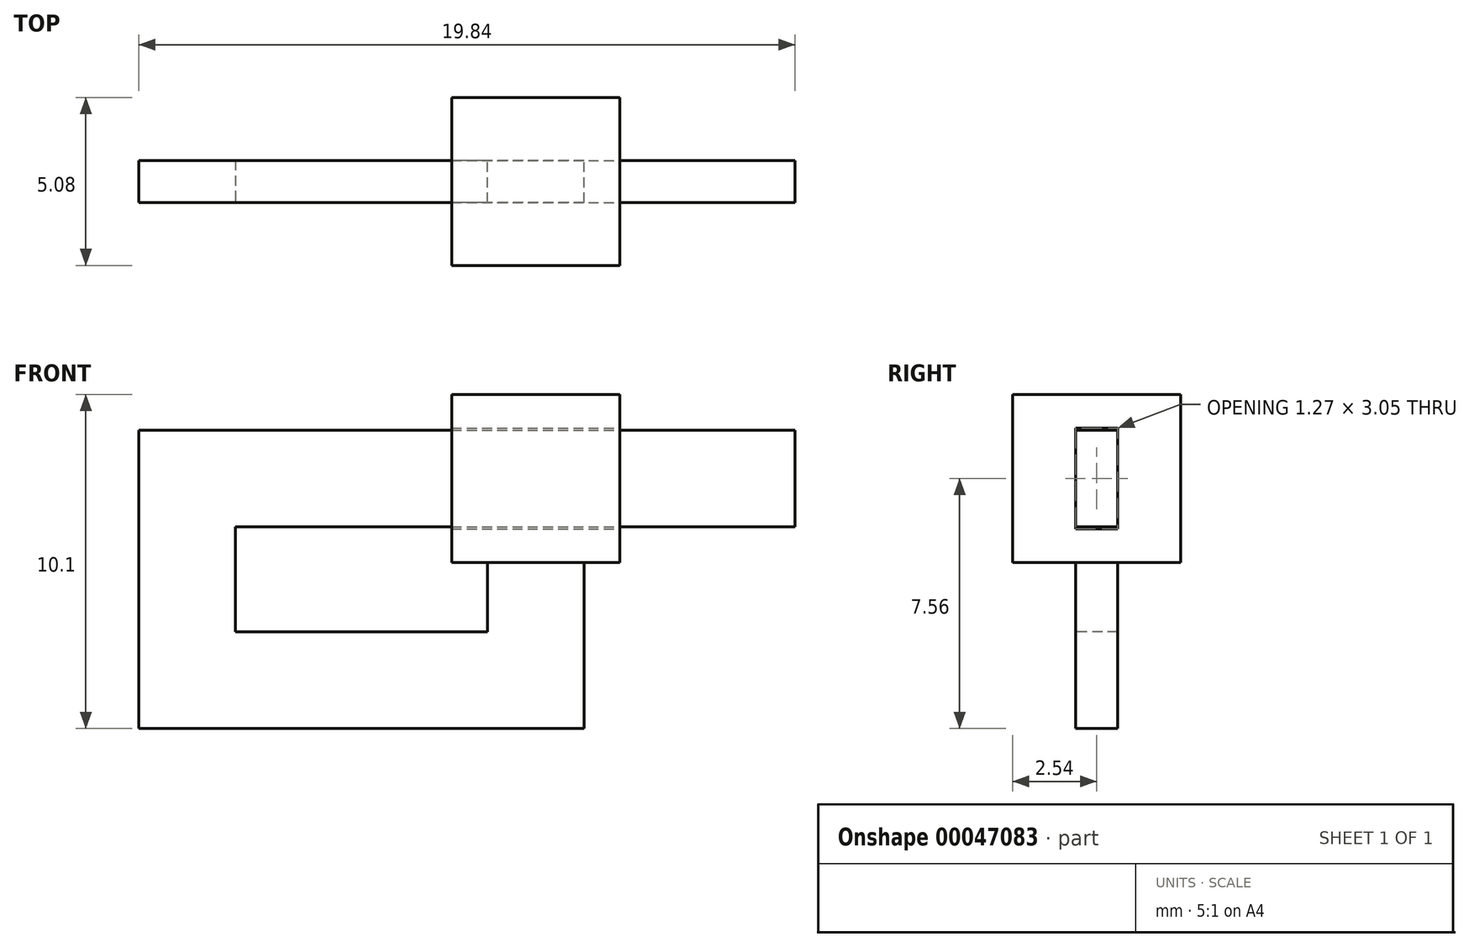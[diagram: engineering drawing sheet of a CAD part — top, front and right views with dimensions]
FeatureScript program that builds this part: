
annotation { "Feature Type Name" : "Feature", "Feature Type Description" : "" }
export const myFeature = defineFeature(function(context is Context, id is Id, definition is map)
    precondition{}
    {
        {
            var Q0;
            Q0=qCreatedBy(makeId("Right.planeOp"),FACE);
            var sketch = newSketch(context, id + "F0", { "sketchPlane" : qUnion([Q0])});
            skLineSegment(sketch, "E0.rect.bottom", {"start": v(-2.54, 2.54) * mm, "end": v(2.54, 2.54) * mm});
            skLineSegment(sketch, "E0.rect.top", {"start": v(-2.54, -2.54) * mm, "end": v(2.54, -2.54) * mm});
            skLineSegment(sketch, "E0.rect.left", {"start": v(-2.54, 2.54) * mm, "end": v(-2.54, -2.54) * mm});
            skLineSegment(sketch, "E0.rect.right", {"start": v(2.54, 2.54) * mm, "end": v(2.54, -2.54) * mm});
            skPoint(sketch, "E0.rect.middle", {"position": v(0, 0) * mm});
            skSolve(sketch);
        }
        {
            var Q0;
            Q0 = qSketchRegion(id + "F0", true);
            extrude(context, id + "F1", {"entities" : qUnion([Q0]), "endBound" : BoundingType.SYMMETRIC, "depth" : 5.08 * mm});
        }
        {
            var Q0;
            Q0=qCreatedBy(makeId("Front.planeOp"),FACE);
            var sketch = newSketch(context, id + "F2", { "sketchPlane" : qUnion([Q0])});
            skPoint(sketch, "E1.orphan", {"position": v(2.54, -2.54) * mm});
            skPoint(sketch, "E2.0.end.orphan", {"position": v(-2.54, -2.54) * mm});
            skPoint(sketch, "E3.start.orphan", {"position": v(-4.53, 0) * mm});
            skPoint(sketch, "E4.start.orphan", {"position": v(0, -2.54) * mm});
            skPoint(sketch, "E5.start.orphan", {"position": v(7.84, 0) * mm});
            skLineSegment(sketch, "E6", {"start": v(7.84, 0) * mm, "end": v(-10.54, 0) * mm});
            skLineSegment(sketch, "E7", {"start": v(-10.54, 0) * mm, "end": v(-10.54, -6.1) * mm});
            skLineSegment(sketch, "E8", {"start": v(-10.54, -6.1) * mm, "end": v(0, -6.1) * mm});
            skLineSegment(sketch, "E9", {"start": v(0, -6.1) * mm, "end": v(0, -2.54) * mm});
            skSolve(sketch);
        }
        {
            var Q0;
            Q0=makeQuery(id+"F1.opExtrude","SWEPT_FACE",FACE,{"disambiguationData":[OSD([sQuery(id+"F0.wireOp",EDGE,"E0.rect.top")])]});
            var sketch = newSketch(context, id + "F3", { "sketchPlane" : qUnion([Q0])});
            skLineSegment(sketch, "E10.rect.bottom", {"start": v(1.46, 0.64) * mm, "end": v(-1.46, 0.64) * mm});
            skLineSegment(sketch, "E10.rect.top", {"start": v(1.46, -0.64) * mm, "end": v(-1.46, -0.64) * mm});
            skLineSegment(sketch, "E10.rect.left", {"start": v(1.46, 0.64) * mm, "end": v(1.46, -0.64) * mm});
            skLineSegment(sketch, "E10.rect.right", {"start": v(-1.46, 0.64) * mm, "end": v(-1.46, -0.64) * mm});
            skPoint(sketch, "E10.rect.middle", {"position": v(0, 0) * mm});
            skSolve(sketch);
        }
        {
            var Q0;
            Q0=makeQuery(id+"F1.opExtrude","CAP_FACE",FACE,{"disambiguationData":[OSD([sQuery(id+"F0.wireOp",EDGE,"E0.rect.bottom"),sQuery(id+"F0.wireOp",EDGE,"E0.rect.top"),sQuery(id+"F0.wireOp",EDGE,"E0.rect.left"),sQuery(id+"F0.wireOp",EDGE,"E0.rect.right")])],"isStart":false});
            var sketch = newSketch(context, id + "F4", { "sketchPlane" : qUnion([Q0])});
            skLineSegment(sketch, "E11.rect.bottom", {"start": v(-0.63, 1.52) * mm, "end": v(0.64, 1.52) * mm});
            skLineSegment(sketch, "E11.rect.top", {"start": v(-0.64, -1.52) * mm, "end": v(0.63, -1.52) * mm});
            skLineSegment(sketch, "E11.rect.left", {"start": v(-0.63, 1.52) * mm, "end": v(-0.64, -1.52) * mm});
            skLineSegment(sketch, "E11.rect.right", {"start": v(0.64, 1.52) * mm, "end": v(0.63, -1.52) * mm});
            skPoint(sketch, "E11.rect.middle", {"position": v(0, 0) * mm});
            skSolve(sketch);
        }
        {
            var Q0;
            Q0 = qSketchRegion(id + "F4", true);
            var Q1;
            Q1=makeQuery(id+"F1.opExtrude","SWEPT_BODY",BODY,{"disambiguationData":[OSD([sQuery(id+"F0.wireOp",EDGE,"E0.rect.bottom"),sQuery(id+"F0.wireOp",EDGE,"E0.rect.top"),sQuery(id+"F0.wireOp",EDGE,"E0.rect.left"),sQuery(id+"F0.wireOp",EDGE,"E0.rect.right")])]});
            extrude(context, id + "F5", {"entities" : qUnion([Q0]), "operationType" : NewBodyOperationType.REMOVE, "endBound" : BoundingType.UP_TO_BODY, "oppositeDirection" : true, "endBoundEntityBody" : qUnion([Q1]), "depth" : 25.4 * mm});
        }
        {
            var Q0;
            Q0 = qSketchRegion(id + "F3", true);
            var Q1;
            Q1=sQuery(id+"F2.wireOp",EDGE,"E9");
            var Q2;
            Q2=sQuery(id+"F2.wireOp",EDGE,"E8");
            var Q3;
            Q3=sQuery(id+"F2.wireOp",EDGE,"E7");
            var Q4;
            Q4=sQuery(id+"F2.wireOp",EDGE,"E6");
            sweep(context, id + "F6", {"operationType" : NewBodyOperationType.ADD, "profiles" : qUnion([Q0]), "path" : qUnion([Q1, Q2, Q3, Q4])});
        }
    });
